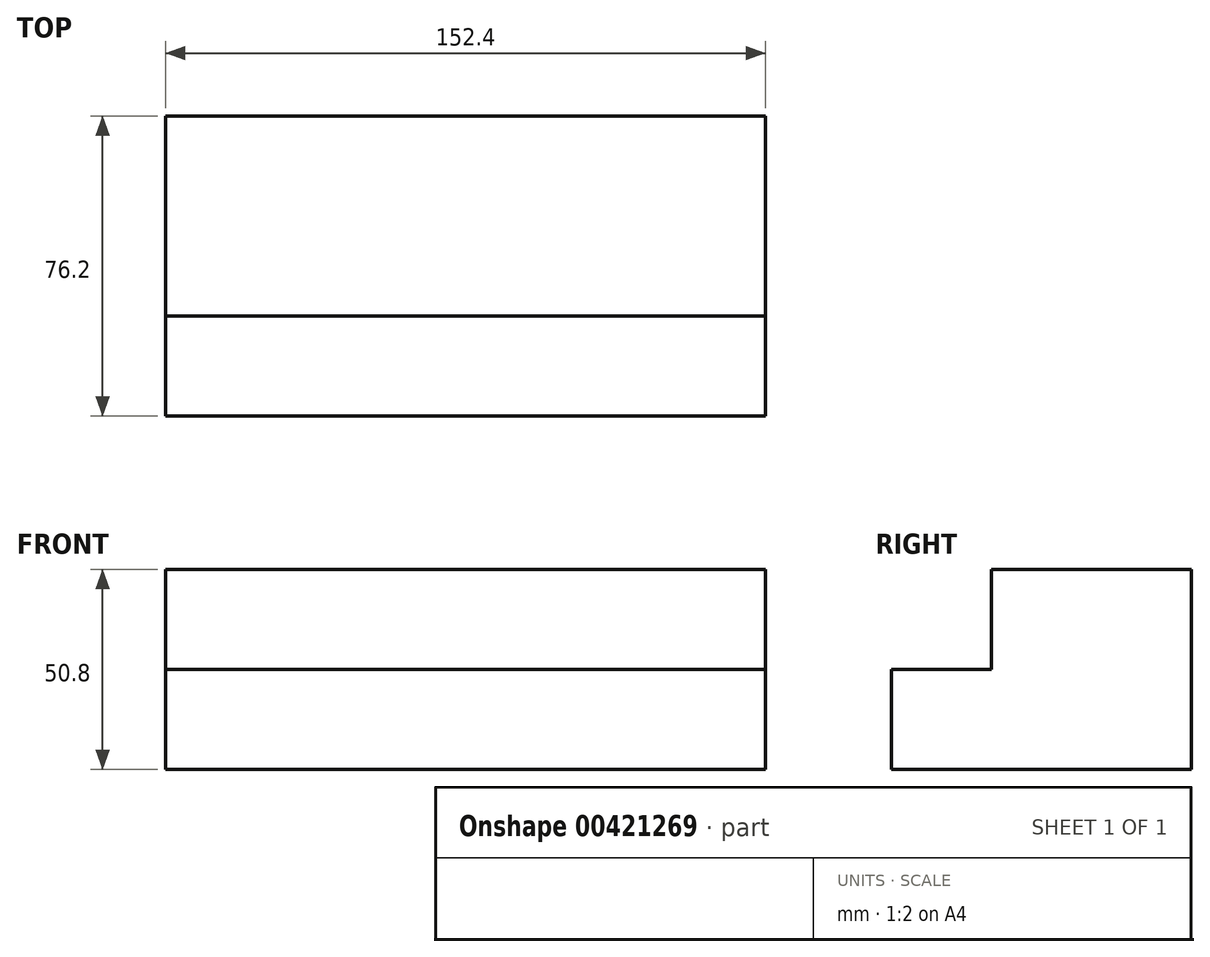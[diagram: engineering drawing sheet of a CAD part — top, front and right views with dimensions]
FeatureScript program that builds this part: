
annotation { "Feature Type Name" : "Feature", "Feature Type Description" : "" }
export const myFeature = defineFeature(function(context is Context, id is Id, definition is map)
    precondition{}
    {
        {
            var Q0;
            Q0=qCreatedBy(makeId("Right.planeOp"),FACE);
            var sketch = newSketch(context, id + "F0", { "sketchPlane" : qUnion([Q0])});
            skLineSegment(sketch, "E0", {"start": v(0, 0) * mm, "end": v(0, 50.8) * mm});
            skLineSegment(sketch, "E1", {"start": v(0, 0) * mm, "end": v(-76.2, 0) * mm});
            skLineSegment(sketch, "E2", {"start": v(0, 50.8) * mm, "end": v(-50.8, 50.8) * mm});
            skLineSegment(sketch, "E3", {"start": v(-50.8, 50.8) * mm, "end": v(-50.8, 25.4) * mm});
            skLineSegment(sketch, "E4", {"start": v(-76.2, 0) * mm, "end": v(-76.2, 25.4) * mm});
            skLineSegment(sketch, "E5", {"start": v(-50.8, 25.4) * mm, "end": v(-76.2, 25.4) * mm});
            skSolve(sketch);
        }
        {
            var Q0;
            Q0=makeQuery(id+"F0.imprint","IMPRINT",FACE,{"disambiguationData":[TD([[makeQuery(id+"F0.imprint","IMPRINT",EDGE,{"derivedFrom":sQuery(id+"F0.wireOp",EDGE,"E0")}),1.0]])]});
            extrude(context, id + "F1", {"entities" : qUnion([Q0]), "depth" : 152.4 * mm});
        }
    });
